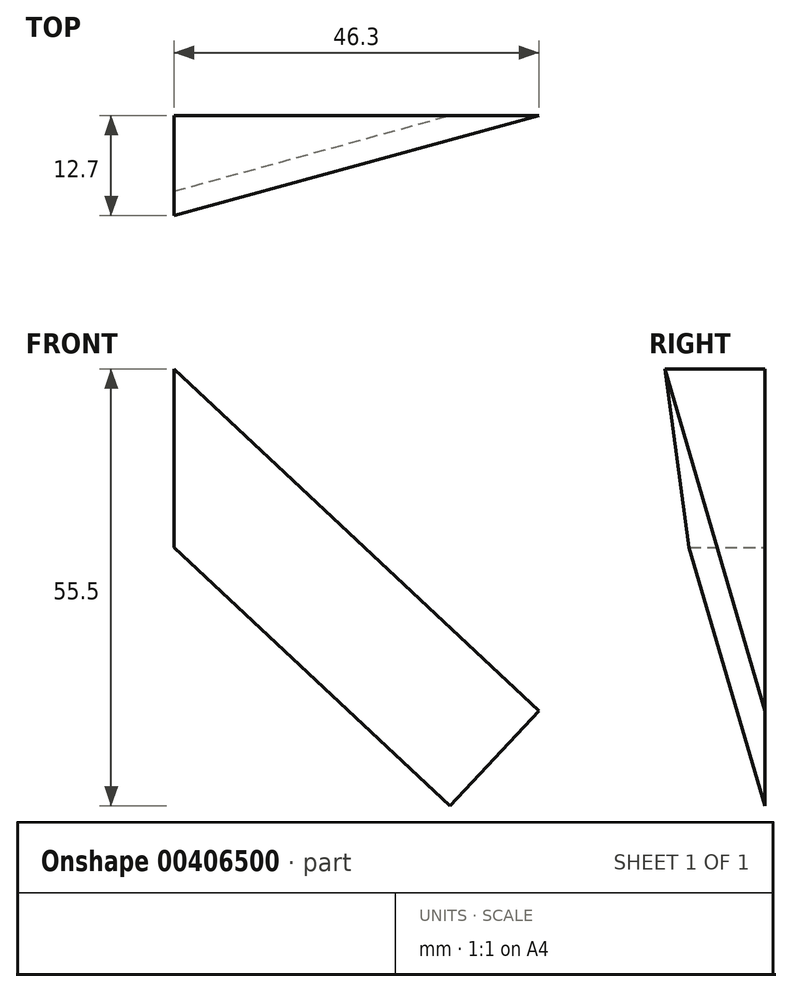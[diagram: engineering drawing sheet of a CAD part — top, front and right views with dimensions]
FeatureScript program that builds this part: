
annotation { "Feature Type Name" : "Feature", "Feature Type Description" : "" }
export const myFeature = defineFeature(function(context is Context, id is Id, definition is map)
    precondition{}
    {
        {
            var Q0;
            Q0=qCreatedBy(makeId("Front.planeOp"),FACE);
            var sketch = newSketch(context, id + "F0", { "sketchPlane" : qUnion([Q0])});
            skLineSegment(sketch, "E0", {"start": v(0, 0) * mm, "end": v(46.3, -43.46) * mm});
            skLineSegment(sketch, "E1", {"start": v(46.3, -43.46) * mm, "end": v(35, -55.5) * mm});
            skLineSegment(sketch, "E2", {"start": v(35, -55.5) * mm, "end": v(0, -22.64) * mm});
            skLineSegment(sketch, "E3", {"start": v(0, -22.64) * mm, "end": v(0, 0) * mm});
            skSolve(sketch);
        }
        {
            var Q0;
            Q0=makeQuery(id+"F0.imprint","IMPRINT",FACE,{"disambiguationData":[TD([[makeQuery(id+"F0.imprint","IMPRINT",EDGE,{"derivedFrom":sQuery(id+"F0.wireOp",EDGE,"E0")}),-1.0]])]});
            extrude(context, id + "F1", {"entities" : qUnion([Q0]), "depth" : 12.7 * mm});
        }
        {
            var Q0;
            Q0=makeQuery(id+"F1.opExtrude","SWEPT_FACE",FACE,{"disambiguationData":[OSD([sQuery(id+"F0.wireOp",EDGE,"E0")])]});
            var sketch = newSketch(context, id + "F2", { "sketchPlane" : qUnion([Q0])});
            skLineSegment(sketch, "E4", {"start": v(63.5, 0) * mm, "end": v(0, -12.7) * mm});
            skSolve(sketch);
        }
        {
            var Q0;
            Q0=makeQuery(id+"F2.imprint","IMPRINT",FACE,{"disambiguationData":[TD([[makeQuery(id+"F2.imprint","IMPRINT",EDGE,{"derivedFrom":sQuery(id+"F2.wireOp",EDGE,"E4")}),1.0]])]});
            extrude(context, id + "F3", {"entities" : qUnion([Q0]), "operationType" : NewBodyOperationType.REMOVE, "endBound" : BoundingType.THROUGH_ALL, "oppositeDirection" : true, "depth" : 25.4 * mm});
        }
    });
